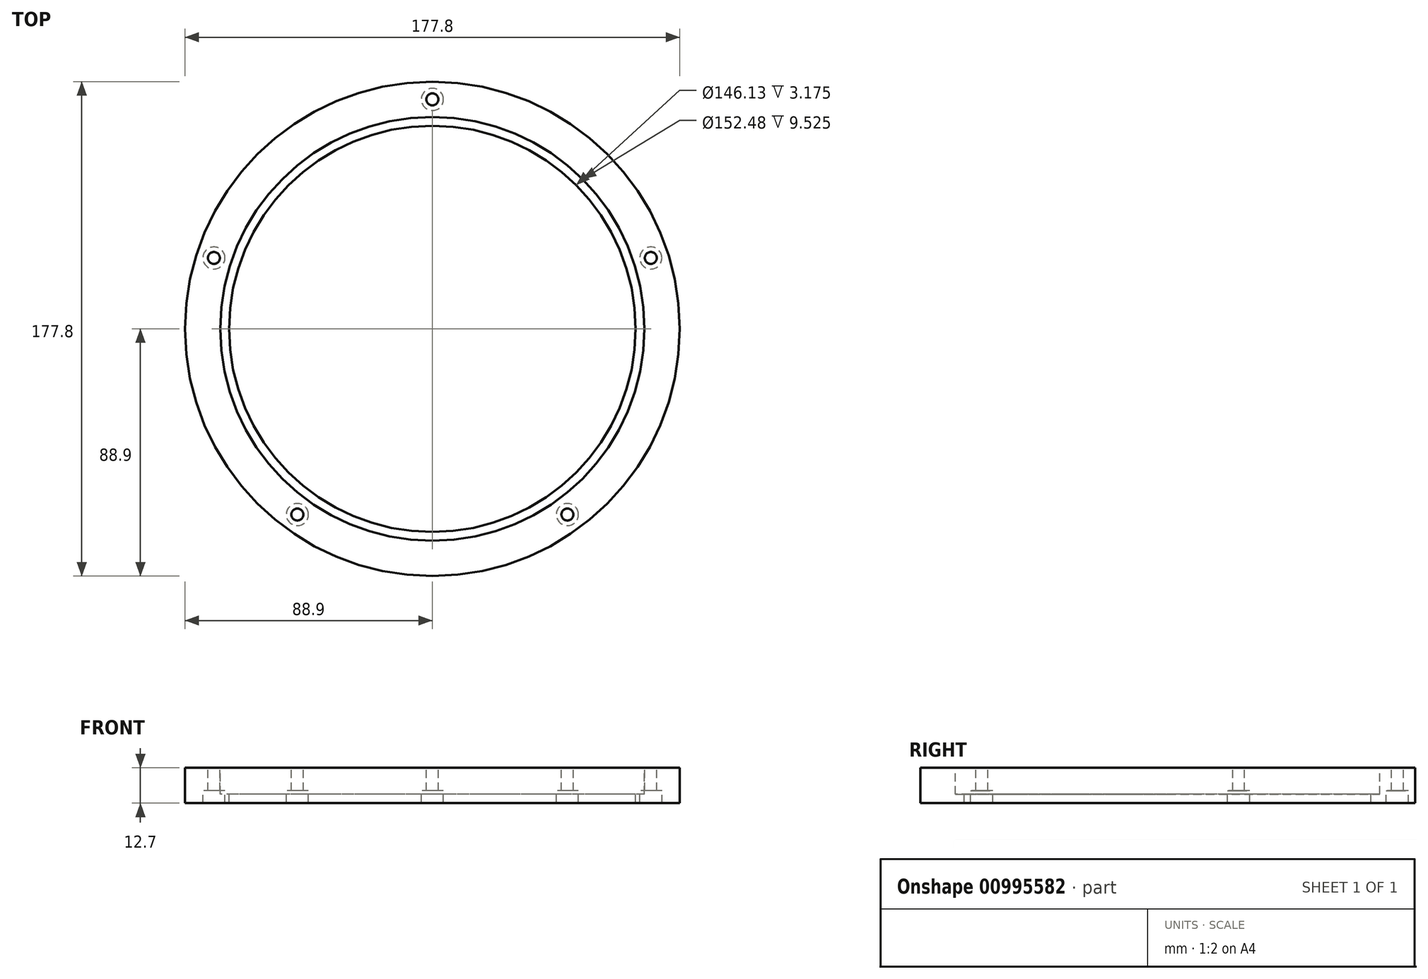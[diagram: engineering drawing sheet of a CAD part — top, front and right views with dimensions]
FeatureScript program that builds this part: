
annotation { "Feature Type Name" : "Feature", "Feature Type Description" : "" }
export const myFeature = defineFeature(function(context is Context, id is Id, definition is map)
    precondition{}
    {
        {
            var Q0;
            Q0=qCreatedBy(makeId("Top.planeOp"),FACE);
            var sketch = newSketch(context, id + "F0", { "sketchPlane" : qUnion([Q0])});
            skCircle(sketch, "E0", {"center": v(0, 0) * mm, "radius": 73.06 * mm});
            skCircle(sketch, "E1", {"center": v(0, 0) * mm, "radius": 76.24 * mm});
            skCircle(sketch, "E2", {"center": v(0, 0) * mm, "radius": 88.9 * mm});
            skCircle(sketch, "E3", {"center": v(0, 0) * mm, "radius": 82.55 * mm, "construction": true});
            skCircle(sketch, "E4", {"center": v(0, 82.55) * mm, "radius": 2.15 * mm});
            skCircle(sketch, "E5", {"center": v(0, 82.55) * mm, "radius": 3.98 * mm});
            skCircle(sketch, "E6.1.0", {"center": v(-78.5, 25.5) * mm, "radius": 2.15 * mm});
            skCircle(sketch, "E6.2.0", {"center": v(-48.52, -66.78) * mm, "radius": 2.15 * mm});
            skCircle(sketch, "E6.3.0", {"center": v(48.52, -66.78) * mm, "radius": 2.15 * mm});
            skCircle(sketch, "E6.4.0", {"center": v(78.5, 25.5) * mm, "radius": 2.15 * mm});
            skCircle(sketch, "E7.1.0", {"center": v(-78.5, 25.5) * mm, "radius": 3.98 * mm});
            skCircle(sketch, "E7.2.0", {"center": v(-48.52, -66.78) * mm, "radius": 3.98 * mm});
            skCircle(sketch, "E7.3.0", {"center": v(48.52, -66.78) * mm, "radius": 3.98 * mm});
            skCircle(sketch, "E7.4.0", {"center": v(78.5, 25.5) * mm, "radius": 3.98 * mm});
            skSolve(sketch);
        }
        {
            var Q0;
            Q0=makeQuery(id+"F0.imprint","IMPRINT",FACE,{"disambiguationData":[TD([[makeQuery(id+"F0.imprint","IMPRINT",EDGE,{"derivedFrom":sQuery(id+"F0.wireOp",EDGE,"E1")}),-1.0]])]});
            var Q1;
            Q1=makeQuery(id+"F0.imprint","IMPRINT",FACE,{"disambiguationData":[TD([[makeQuery(id+"F0.imprint","IMPRINT",EDGE,{"derivedFrom":sQuery(id+"F0.wireOp",EDGE,"E0")}),-1.0]])]});
            extrude(context, id + "F1", {"entities" : qUnion([Q0, Q1]), "oppositeDirection" : true, "depth" : 12.7 * mm, "offsetDistance" : 25.4 * mm});
        }
        {
            var Q0;
            Q0=makeQuery(id+"F0.imprint","IMPRINT",FACE,{"disambiguationData":[TD([[makeQuery(id+"F0.imprint","IMPRINT",EDGE,{"derivedFrom":sQuery(id+"F0.wireOp",EDGE,"E0")}),-1.0]])]});
            extrude(context, id + "F2", {"entities" : qUnion([Q0]), "operationType" : NewBodyOperationType.REMOVE, "oppositeDirection" : true, "depth" : 9.52 * mm, "offsetDistance" : 25.4 * mm});
        }
        {
            var Q0;
            Q0=makeQuery(id+"F0.imprint","IMPRINT",FACE,{"disambiguationData":[TD([[makeQuery(id+"F0.imprint","IMPRINT",EDGE,{"derivedFrom":sQuery(id+"F0.wireOp",EDGE,"E6.2.0")}),-1.0]])]});
            var Q1;
            Q1=makeQuery(id+"F0.imprint","IMPRINT",FACE,{"disambiguationData":[TD([[makeQuery(id+"F0.imprint","IMPRINT",EDGE,{"derivedFrom":sQuery(id+"F0.wireOp",EDGE,"E6.3.0")}),-1.0]])]});
            var Q2;
            Q2=makeQuery(id+"F0.imprint","IMPRINT",FACE,{"disambiguationData":[TD([[makeQuery(id+"F0.imprint","IMPRINT",EDGE,{"derivedFrom":sQuery(id+"F0.wireOp",EDGE,"E6.4.0")}),-1.0]])]});
            var Q3;
            Q3=makeQuery(id+"F0.imprint","IMPRINT",FACE,{"disambiguationData":[TD([[makeQuery(id+"F0.imprint","IMPRINT",EDGE,{"derivedFrom":sQuery(id+"F0.wireOp",EDGE,"E4")}),-1.0]])]});
            var Q4;
            Q4=makeQuery(id+"F0.imprint","IMPRINT",FACE,{"disambiguationData":[TD([[makeQuery(id+"F0.imprint","IMPRINT",EDGE,{"derivedFrom":sQuery(id+"F0.wireOp",EDGE,"E6.1.0")}),-1.0]])]});
            extrude(context, id + "F3", {"entities" : qUnion([Q0, Q1, Q2, Q3, Q4]), "operationType" : NewBodyOperationType.ADD, "oppositeDirection" : true, "depth" : 8.25 * mm, "offsetDistance" : 25.4 * mm});
        }
    });
